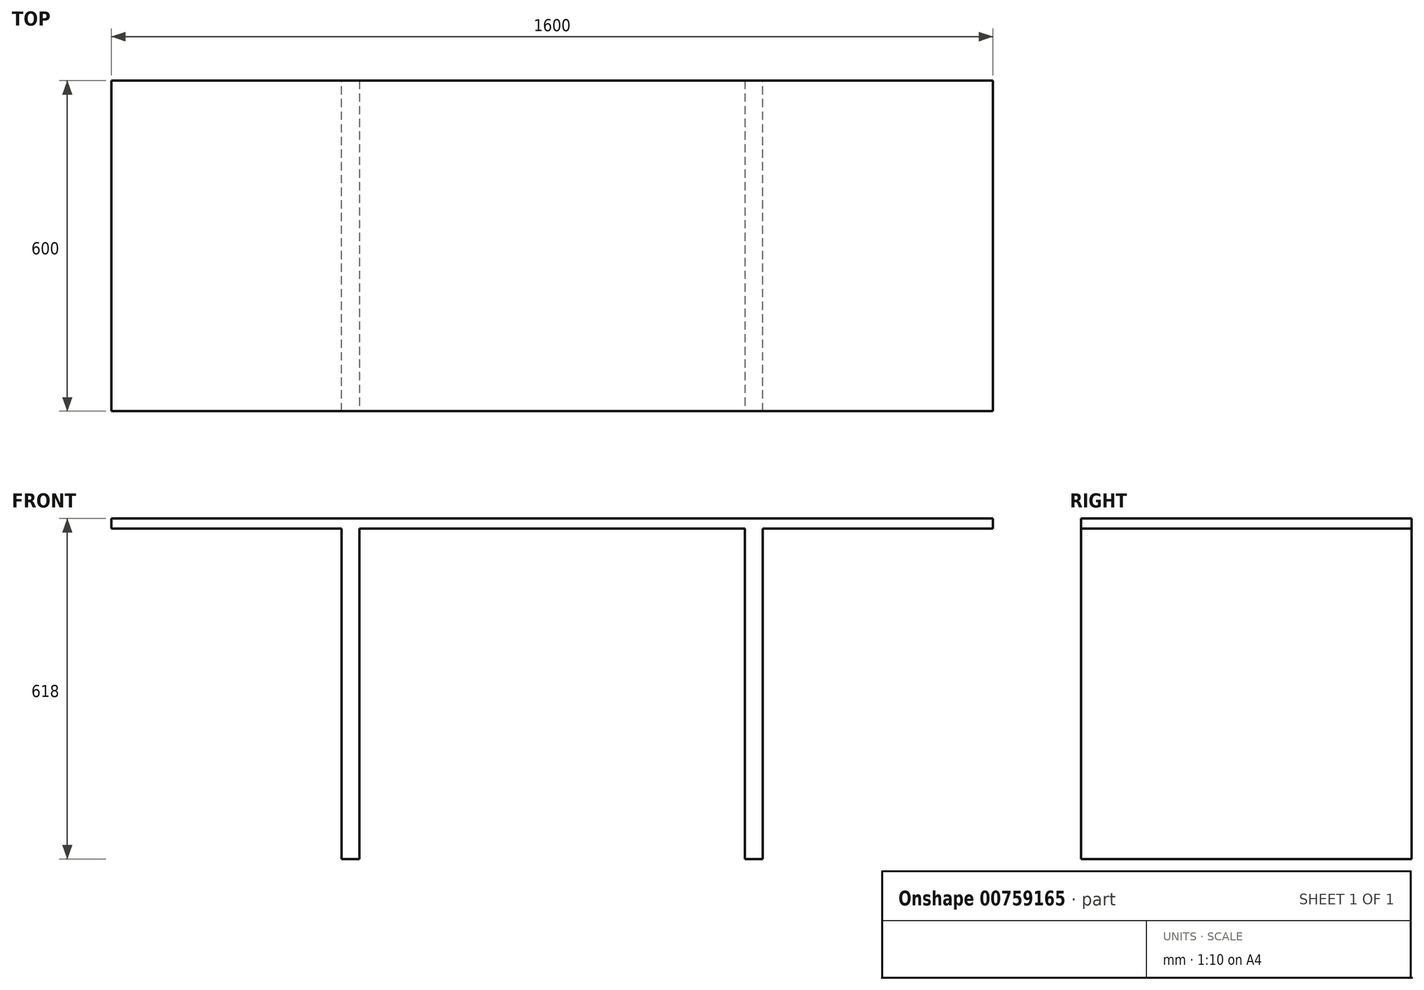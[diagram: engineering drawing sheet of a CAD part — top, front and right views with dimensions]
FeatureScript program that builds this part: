
annotation { "Feature Type Name" : "Feature", "Feature Type Description" : "" }
export const myFeature = defineFeature(function(context is Context, id is Id, definition is map)
    precondition{}
    {
        {
            var Q0;
            Q0=qCreatedBy(makeId("Top.planeOp"),FACE);
            var sketch = newSketch(context, id + "F0", { "sketchPlane" : qUnion([Q0])});
            skLineSegment(sketch, "E0.bottom", {"start": v(800, -300) * mm, "end": v(-800, -300) * mm});
            skLineSegment(sketch, "E0.top", {"start": v(800, 300) * mm, "end": v(-800, 300) * mm});
            skLineSegment(sketch, "E0.left", {"start": v(800, -300) * mm, "end": v(800, 300) * mm});
            skLineSegment(sketch, "E0.right", {"start": v(-800, -300) * mm, "end": v(-800, 300) * mm});
            skPoint(sketch, "E0.middle", {"position": v(0, 0) * mm});
            skLineSegment(sketch, "E1.bottom", {"start": v(350, 300) * mm, "end": v(-350, 300) * mm});
            skLineSegment(sketch, "E1.top", {"start": v(350, -300) * mm, "end": v(-350, -300) * mm});
            skLineSegment(sketch, "E1.left", {"start": v(350, 300) * mm, "end": v(350, -300) * mm});
            skLineSegment(sketch, "E1.right", {"start": v(-350, 300) * mm, "end": v(-350, -300) * mm});
            skLineSegment(sketch, "E2.bottom", {"start": v(-350, -300) * mm, "end": v(-382.56, -300) * mm});
            skLineSegment(sketch, "E2.top", {"start": v(-350, 300) * mm, "end": v(-382.56, 300) * mm});
            skLineSegment(sketch, "E2.left", {"start": v(-350, -300) * mm, "end": v(-350, 300) * mm});
            skLineSegment(sketch, "E2.right", {"start": v(-382.56, -300) * mm, "end": v(-382.56, 300) * mm});
            skLineSegment(sketch, "E3.bottom", {"start": v(350, -300) * mm, "end": v(382.56, -300) * mm});
            skLineSegment(sketch, "E3.top", {"start": v(350, 300) * mm, "end": v(382.56, 300) * mm});
            skLineSegment(sketch, "E3.left", {"start": v(350, -300) * mm, "end": v(350, 300) * mm});
            skLineSegment(sketch, "E3.right", {"start": v(382.56, -300) * mm, "end": v(382.56, 300) * mm});
            skSolve(sketch);
        }
        {
            var Q0;
            {var subQ0=sQuery(id+"F0.wireOp",EDGE,"E1.left");var subQ3=sQuery(id+"F0.wireOp",EDGE,"E1.right");var subQ8=makeQuery(id+"F0.imprint","IMPRINT",EDGE,{"derivedFrom":subQ0});var subQ9=makeQuery(id+"F0.imprint","IMPRINT",EDGE,{"derivedFrom":subQ3});var subQ10=sQuery(id+"F0.wireOp",EDGE,"E0.left");var subQ19=sQuery(id+"F0.wireOp",EDGE,"E0.right");Q0=qUnion([makeQuery(id+"F0.imprint","IMPRINT",FACE,{"disambiguationData":[TD([[subQ8,1.0]])]}),makeQuery(id+"F0.imprint","IMPRINT",FACE,{"disambiguationData":[TD([[makeQuery(id+"F0.imprint","IMPRINT",EDGE,{"derivedFrom":subQ19}),-1.0]])]}),makeQuery(id+"F0.imprint","IMPRINT",FACE,{"disambiguationData":[TD([[subQ9,-1.0]])]}),makeQuery(id+"F0.imprint","IMPRINT",FACE,{"disambiguationData":[TD([[makeQuery(id+"F0.imprint","IMPRINT",EDGE,{"derivedFrom":subQ10}),1.0]])]}),makeQuery(id+"F0.imprint","IMPRINT",FACE,{"disambiguationData":[TD([[subQ8,-1.0]])]})]);}
            extrude(context, id + "F1", {"entities" : qUnion([Q0]), "depth" : 18 * mm, "offsetDistance" : 25 * mm});
        }
        {
            var Q0;
            {var subQ2=sQuery(id+"F0.wireOp",EDGE,"E1.right");Q0=makeQuery(id+"F0.imprint","IMPRINT",FACE,{"disambiguationData":[TD([[makeQuery(id+"F0.imprint","IMPRINT",EDGE,{"derivedFrom":subQ2}),-1.0]])]});}
            var Q1;
            {var subQ0=sQuery(id+"F0.wireOp",EDGE,"E1.left");Q1=makeQuery(id+"F0.imprint","IMPRINT",FACE,{"disambiguationData":[TD([[makeQuery(id+"F0.imprint","IMPRINT",EDGE,{"derivedFrom":subQ0}),1.0]])]});}
            extrude(context, id + "F2", {"entities" : qUnion([Q0, Q1]), "operationType" : NewBodyOperationType.ADD, "oppositeDirection" : true, "depth" : 600 * mm, "offsetDistance" : 25 * mm});
        }
    });
